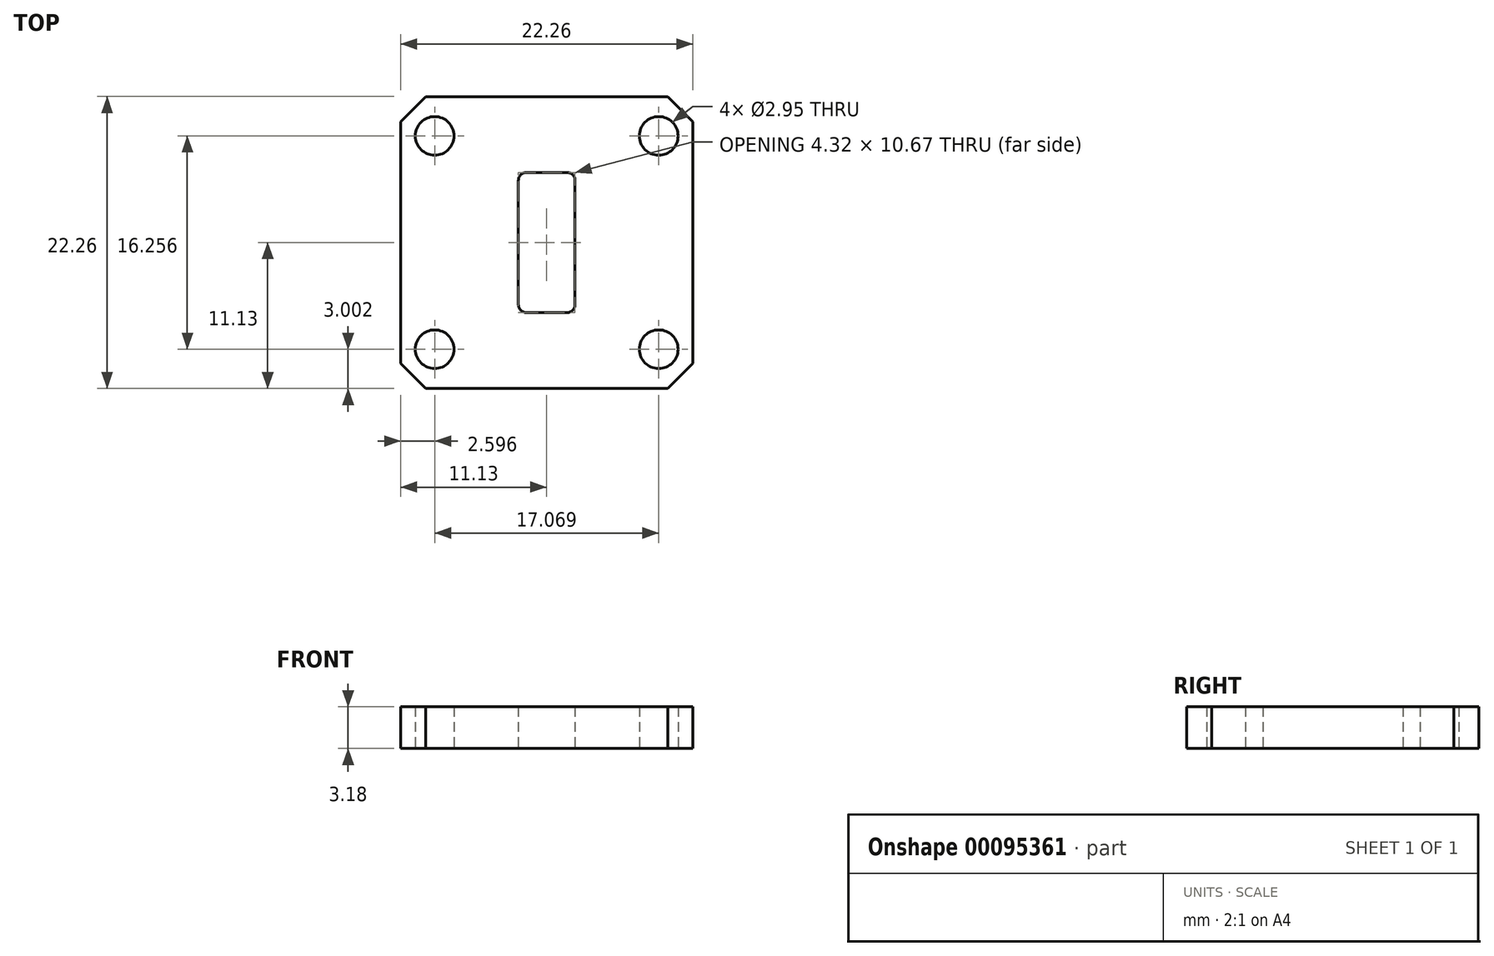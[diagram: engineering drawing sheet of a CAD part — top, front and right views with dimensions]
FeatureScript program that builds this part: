
annotation { "Feature Type Name" : "Feature", "Feature Type Description" : "" }
export const myFeature = defineFeature(function(context is Context, id is Id, definition is map)
    precondition{}
    {
        {
            var Q0;
            Q0=qCreatedBy(makeId("Top.planeOp"),FACE);
            var sketch = newSketch(context, id + "F0", { "sketchPlane" : qUnion([Q0])});
            skLineSegment(sketch, "E0.bottom", {"start": v(-11.13, 11.13) * mm, "end": v(11.13, 11.13) * mm});
            skLineSegment(sketch, "E0.top", {"start": v(-11.13, -11.13) * mm, "end": v(11.13, -11.13) * mm});
            skLineSegment(sketch, "E0.left", {"start": v(-11.13, 11.13) * mm, "end": v(-11.13, -11.13) * mm});
            skLineSegment(sketch, "E0.right", {"start": v(11.13, 11.13) * mm, "end": v(11.13, -11.13) * mm});
            skPoint(sketch, "E0.middle", {"position": v(0, 0) * mm});
            skLineSegment(sketch, "E1.bottom", {"start": v(-2.16, 5.33) * mm, "end": v(2.16, 5.33) * mm});
            skLineSegment(sketch, "E1.top", {"start": v(-2.16, -5.33) * mm, "end": v(2.16, -5.33) * mm});
            skLineSegment(sketch, "E1.left", {"start": v(-2.16, 5.33) * mm, "end": v(-2.16, -5.33) * mm});
            skLineSegment(sketch, "E1.right", {"start": v(2.16, 5.33) * mm, "end": v(2.16, -5.33) * mm});
            skCircle(sketch, "E2", {"center": v(-8.53, 8.13) * mm, "radius": 1.47 * mm});
            skCircle(sketch, "E3", {"center": v(8.53, 8.13) * mm, "radius": 1.47 * mm});
            skCircle(sketch, "E4", {"center": v(-8.53, -8.13) * mm, "radius": 1.47 * mm});
            skCircle(sketch, "E5", {"center": v(8.53, -8.13) * mm, "radius": 1.47 * mm});
            skSolve(sketch);
        }
        {
            var Q0;
            Q0=makeQuery(id+"F0.imprint","IMPRINT",FACE,{"disambiguationData":[TD([[makeQuery(id+"F0.imprint","IMPRINT",EDGE,{"derivedFrom":sQuery(id+"F0.wireOp",EDGE,"E0.bottom")}),-1.0]])]});
            extrude(context, id + "F1", {"entities" : qUnion([Q0]), "depth" : 3.17 * mm});
        }
        {
            var Q0;
            Q0=makeQuery(id+"F1.opExtrude","SWEPT_EDGE",EDGE,{"disambiguationData":[OSD([sQuery(id+"F0.wireOp",EDGE,"E0.top"),sQuery(id+"F0.wireOp",EDGE,"E0.left")])]});
            var Q1;
            Q1=makeQuery(id+"F1.opExtrude","SWEPT_EDGE",EDGE,{"disambiguationData":[OSD([sQuery(id+"F0.wireOp",EDGE,"E0.bottom"),sQuery(id+"F0.wireOp",EDGE,"E0.left")])]});
            var Q2;
            Q2=makeQuery(id+"F1.opExtrude","SWEPT_EDGE",EDGE,{"disambiguationData":[OSD([sQuery(id+"F0.wireOp",EDGE,"E0.bottom"),sQuery(id+"F0.wireOp",EDGE,"E0.right")])]});
            var Q3;
            Q3=makeQuery(id+"F1.opExtrude","SWEPT_EDGE",EDGE,{"disambiguationData":[OSD([sQuery(id+"F0.wireOp",EDGE,"E0.top"),sQuery(id+"F0.wireOp",EDGE,"E0.right")])]});
            chamfer(context, id + "F2", {"entities" : qUnion([Q0, Q1, Q2, Q3]), "width" : 1.9 * mm, "tangentPropagation" : true});
        }
        {
            var Q0;
            Q0=makeQuery(id+"F1.opExtrude","SWEPT_EDGE",EDGE,{"disambiguationData":[OSD([sQuery(id+"F0.wireOp",EDGE,"E1.top"),sQuery(id+"F0.wireOp",EDGE,"E1.right")])]});
            var Q1;
            Q1=makeQuery(id+"F1.opExtrude","SWEPT_EDGE",EDGE,{"disambiguationData":[OSD([sQuery(id+"F0.wireOp",EDGE,"E1.top"),sQuery(id+"F0.wireOp",EDGE,"E1.left")])]});
            var Q2;
            Q2=makeQuery(id+"F1.opExtrude","SWEPT_EDGE",EDGE,{"disambiguationData":[OSD([sQuery(id+"F0.wireOp",EDGE,"E1.bottom"),sQuery(id+"F0.wireOp",EDGE,"E1.left")])]});
            var Q3;
            Q3=makeQuery(id+"F1.opExtrude","SWEPT_EDGE",EDGE,{"disambiguationData":[OSD([sQuery(id+"F0.wireOp",EDGE,"E1.bottom"),sQuery(id+"F0.wireOp",EDGE,"E1.right")])]});
            fillet(context, id + "F3", {"entities" : qUnion([Q0, Q1, Q2, Q3]), "radius" : 0.6 * mm, "tangentPropagation" : true, "allowEdgeOverflow" : false});
        }
    });
